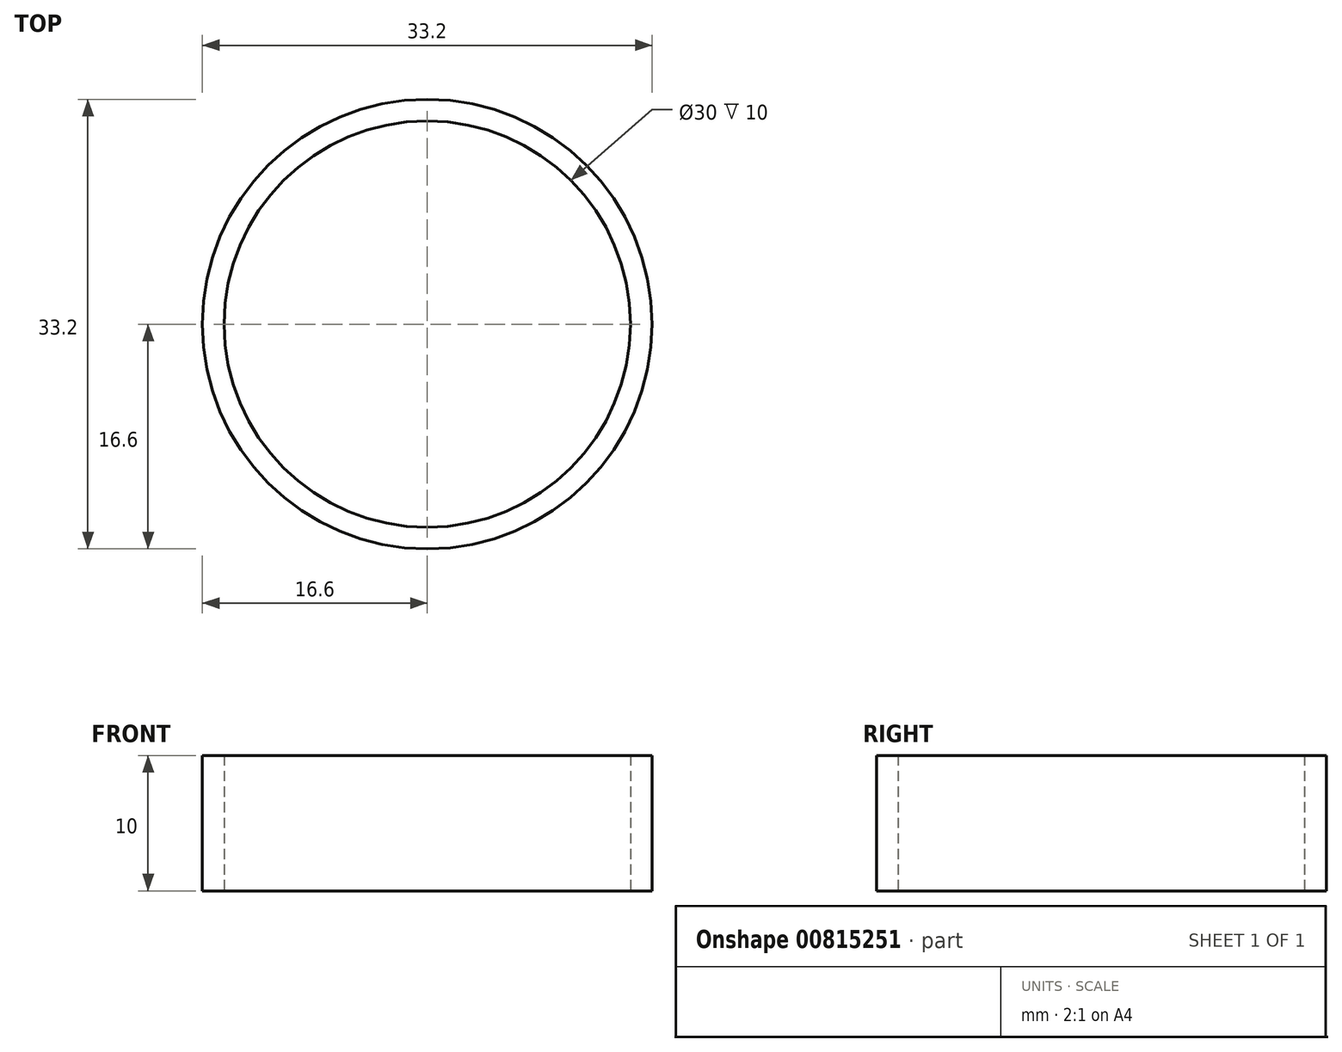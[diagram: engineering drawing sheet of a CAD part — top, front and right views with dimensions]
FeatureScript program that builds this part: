
annotation { "Feature Type Name" : "Feature", "Feature Type Description" : "" }
export const myFeature = defineFeature(function(context is Context, id is Id, definition is map)
    precondition{}
    {
        {
            var Q0;
            Q0=qCreatedBy(makeId("Top.planeOp"),FACE);
            var sketch = newSketch(context, id + "F0", { "sketchPlane" : qUnion([Q0])});
            skCircle(sketch, "E0", {"center": v(0, 0) * mm, "radius": 15 * mm});
            skCircle(sketch, "E1", {"center": v(0, 0) * mm, "radius": 16.6 * mm});
            skSolve(sketch);
        }
        {
            var Q0;
            Q0=makeQuery(id+"F0.imprint","IMPRINT",FACE,{"disambiguationData":[TD([[makeQuery(id+"F0.imprint","IMPRINT",EDGE,{"derivedFrom":sQuery(id+"F0.wireOp",EDGE,"E0")}),-1.0]])]});
            extrude(context, id + "F1", {"entities" : qUnion([Q0]), "depth" : 10 * mm, "offsetDistance" : 25 * mm});
        }
    });
